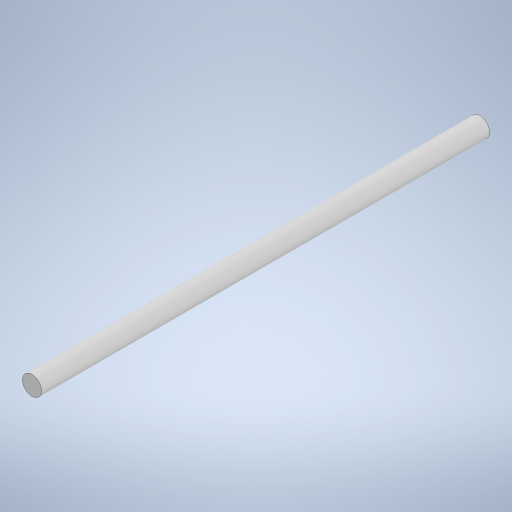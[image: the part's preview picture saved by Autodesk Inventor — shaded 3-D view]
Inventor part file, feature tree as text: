
AUTODESK INVENTOR PART (.ipt)
format: ipt  version: 2023 (Build 270158000, 158)  size: 230,912 bytes
history: native  units: in
note: dims shown in document units (in); Inventor stores cm internally (conversion verified against a paired STEP export)
features: extrude x1, sketch x1
ambient origin geometry x8: Origin, YZ Plane, XZ Plane, XY Plane, X Axis, Y Axis, Z Axis, Center Point
bodies: Solid1 (feature_tree)
feature tree (2):
  extrude  "Extrusion1"  Depth=9.252in TaperAngle=0.0deg
  sketch  "Sketch1"  dims[d0=0.3937in d1=9.252in d2=0.0in]
